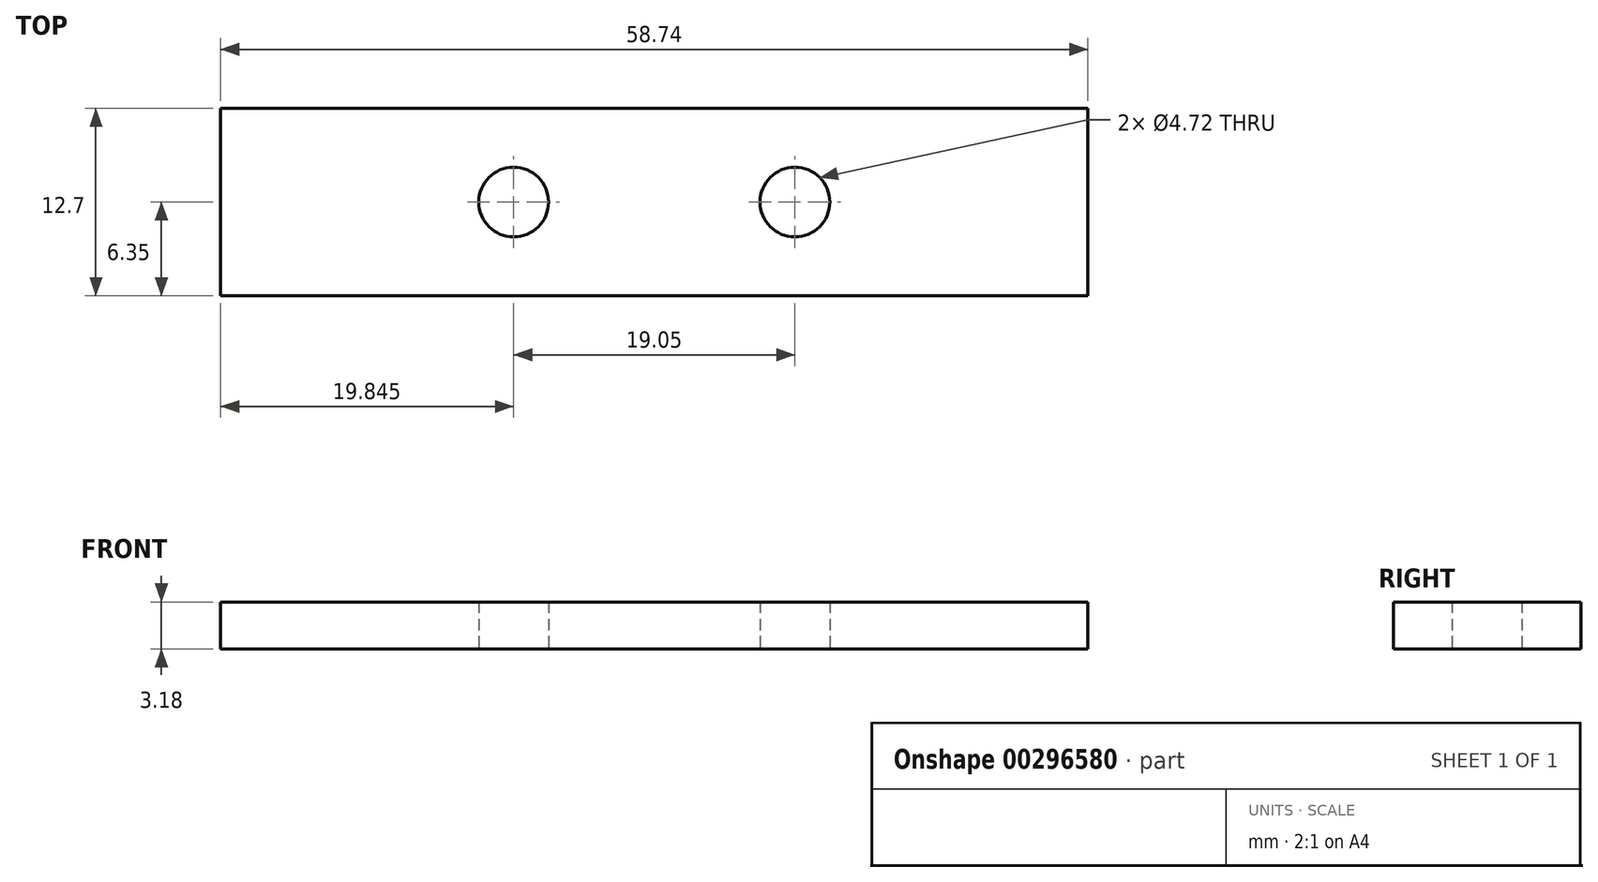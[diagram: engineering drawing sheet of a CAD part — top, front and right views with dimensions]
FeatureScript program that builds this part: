
annotation { "Feature Type Name" : "Feature", "Feature Type Description" : "" }
export const myFeature = defineFeature(function(context is Context, id is Id, definition is map)
    precondition{}
    {
        {
            var Q0;
            Q0=qCreatedBy(makeId("Top.planeOp"),FACE);
            var sketch = newSketch(context, id + "F0", { "sketchPlane" : qUnion([Q0])});
            skLineSegment(sketch, "E0.bottom", {"start": v(29.37, -6.35) * mm, "end": v(-29.37, -6.35) * mm});
            skLineSegment(sketch, "E0.top", {"start": v(29.37, 6.35) * mm, "end": v(-29.37, 6.35) * mm});
            skLineSegment(sketch, "E0.left", {"start": v(29.37, -6.35) * mm, "end": v(29.37, 6.35) * mm});
            skLineSegment(sketch, "E0.right", {"start": v(-29.37, -6.35) * mm, "end": v(-29.37, 6.35) * mm});
            skPoint(sketch, "E0.middle", {"position": v(0, 0) * mm});
            skLineSegment(sketch, "E1", {"start": v(-9.53, 0) * mm, "end": v(9.53, 0) * mm, "construction": true});
            skCircle(sketch, "E2", {"center": v(9.53, 0) * mm, "radius": 2.36 * mm});
            skCircle(sketch, "E3", {"center": v(-9.53, 0) * mm, "radius": 2.36 * mm});
            skSolve(sketch);
        }
        {
            var Q0;
            Q0 = qSketchRegion(id + "F0", true);
            extrude(context, id + "F1", {"entities" : qUnion([Q0]), "depth" : 3.17 * mm});
        }
    });
